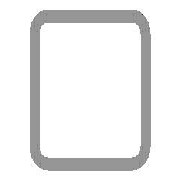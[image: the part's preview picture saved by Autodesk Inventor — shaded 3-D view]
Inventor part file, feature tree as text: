
AUTODESK INVENTOR PART (.ipt)
format: ipt  version: 2019 (Build 230136000, 136)  size: 129,536 bytes
history: native  units: mm (DEFAULTED — no unit token found)
features: other x4, sketch x3, plane x1
ambient origin geometry x8: Origin, YZ Plane, XZ Plane, XY Plane, X Axis, Y Axis, Z Axis, Center Point
bodies: Solid1 (feature_tree), Body (feature_tree)
feature tree (8):
  parser-record x1  (decoder bookkeeping rows leaked as tree rows — omitted from the tree; the rows remain in map.json)
  other  "Driven Length"
  other  "Start plane"
  other  "End plane"
  sketch  "Sketch"  dims[d7=4.0mm d9=20.0mm d11=20.0mm d12=2.0mm d13=-0.0mm d14=300.0mm d15=10.0mm d16=10.0mm d17=90.0deg d18=300.0mm]
  sketch  "Sketch3"  dims[d3=300.0mm]
  plane  "Work Plane3"
  sketch  "Sketch4"  dims[d4=0.0mm]
